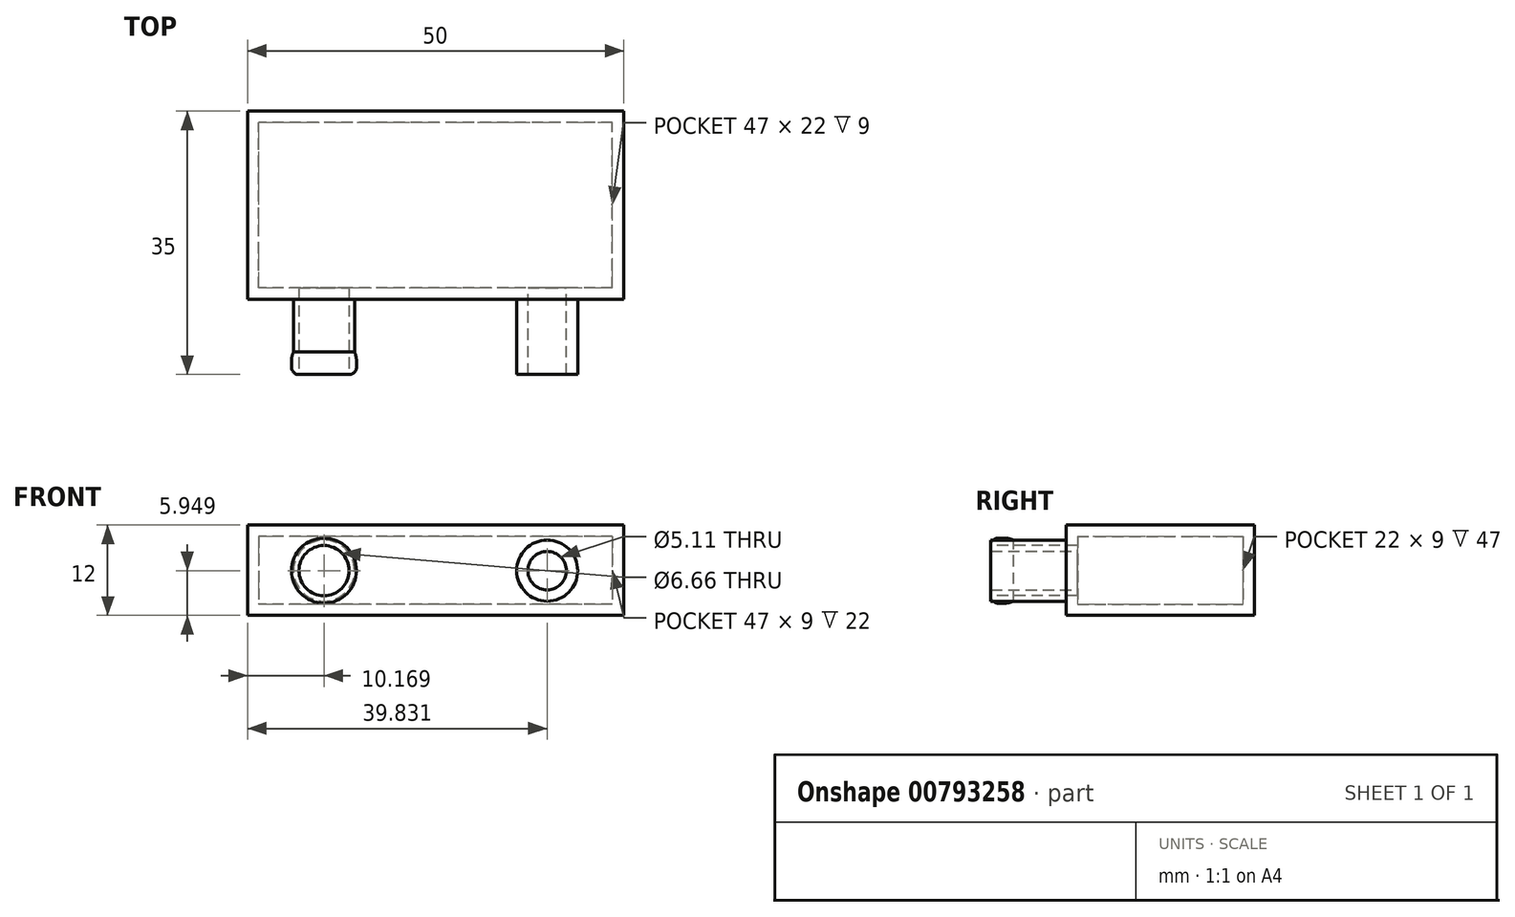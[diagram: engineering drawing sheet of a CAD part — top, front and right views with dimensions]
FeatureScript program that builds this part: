
annotation { "Feature Type Name" : "Feature", "Feature Type Description" : "" }
export const myFeature = defineFeature(function(context is Context, id is Id, definition is map)
    precondition{}
    {
        {
            var Q0;
            Q0=qCreatedBy(makeId("Top.planeOp"),FACE);
            var sketch = newSketch(context, id + "F0", { "sketchPlane" : qUnion([Q0])});
            skLineSegment(sketch, "E0.bottom", {"start": v(25, -12.5) * mm, "end": v(-25, -12.5) * mm});
            skLineSegment(sketch, "E0.top", {"start": v(25, 12.5) * mm, "end": v(-25, 12.5) * mm});
            skLineSegment(sketch, "E0.left", {"start": v(25, -12.5) * mm, "end": v(25, 12.5) * mm});
            skLineSegment(sketch, "E0.right", {"start": v(-25, -12.5) * mm, "end": v(-25, 12.5) * mm});
            skPoint(sketch, "E0.middle", {"position": v(0, 0) * mm});
            skSolve(sketch);
        }
        {
            var Q0;
            Q0 = qSketchRegion(id + "F0", true);
            extrude(context, id + "F1", {"entities" : qUnion([Q0]), "depth" : 12 * mm, "offsetDistance" : 25 * mm});
        }
        {
            var Q0;
            Q0=makeQuery(id+"F1.opExtrude","SWEPT_FACE",FACE,{"disambiguationData":[OSD([sQuery(id+"F0.wireOp",EDGE,"E0.bottom")])]});
            var sketch = newSketch(context, id + "F2", { "sketchPlane" : qUnion([Q0])});
            skCircle(sketch, "E1", {"center": v(-14.83, 5.95) * mm, "radius": 4.05 * mm});
            skLineSegment(sketch, "E2", {"start": v(0, 20.65) * mm, "end": v(0, -15.35) * mm, "construction": true});
            skCircle(sketch, "E3.MirrorC", {"center": v(14.83, 5.95) * mm, "radius": 4.05 * mm});
            skSolve(sketch);
        }
        {
            var Q0;
            Q0 = qSketchRegion(id + "F2", true);
            extrude(context, id + "F3", {"entities" : qUnion([Q0]), "operationType" : NewBodyOperationType.ADD, "depth" : 10 * mm, "offsetDistance" : 25 * mm});
        }
        {
            var Q0;
            Q0=makeQuery(id+"F3.opExtrude","CAP_FACE",FACE,{"disambiguationData":[OSD([sQuery(id+"F2.wireOp",EDGE,"E3.MirrorC")])],"isStart":false});
            var Q1;
            Q1=makeQuery(id+"F3.opExtrude","CAP_FACE",FACE,{"disambiguationData":[OSD([sQuery(id+"F2.wireOp",EDGE,"E1")])],"isStart":false});
            shell(context, id + "F4", {"entities" : qUnion([Q0, Q1]), "thickness" : 1.5 * mm});
        }
        {
            var Q0;
            Q0=makeQuery(id+"F3.opExtrude","CAP_FACE",FACE,{"disambiguationData":[OSD([sQuery(id+"F2.wireOp",EDGE,"E1")])],"isStart":false});
            var sketch = newSketch(context, id + "F5", { "sketchPlane" : qUnion([Q0])});
            skCircle(sketch, "E4", {"center": v(-14.83, 5.95) * mm, "radius": 4.33 * mm});
            skSolve(sketch);
        }
        {
            var Q0;
            Q0 = qSketchRegion(id + "F5", true);
            extrude(context, id + "F6", {"entities" : qUnion([Q0]), "operationType" : NewBodyOperationType.ADD, "oppositeDirection" : true, "depth" : 3 * mm, "offsetDistance" : 25 * mm});
        }
        {
            var Q0;
            Q0=makeQuery(id+"F6.opExtrude","CAP_EDGE",EDGE,{"disambiguationData":[OSD([sQuery(id+"F5.wireOp",EDGE,"E4")])],"isStart":false});
            fillet(context, id + "F7", {"entities" : qUnion([Q0]), "radius" : 3 * mm, "tangentPropagation" : true, "allowEdgeOverflow" : false});
        }
        {
            var Q0;
            Q0=makeQuery(id+"F6.opExtrude","CAP_EDGE",EDGE,{"disambiguationData":[OSD([sQuery(id+"F5.wireOp",EDGE,"E4")])],"isStart":true});
            fillet(context, id + "F8", {"entities" : qUnion([Q0]), "radius" : 1 * mm, "tangentPropagation" : true, "allowEdgeOverflow" : false});
        }
        {
            var Q0;
            Q0=makeQuery(id+"F6.boolean.opBoolean","MERGE",FACE,{"derivedFrom":[makeQuery(id+"F3.opExtrude","CAP_FACE",FACE,{"disambiguationData":[OSD([sQuery(id+"F2.wireOp",EDGE,"E1")])],"isStart":false}),makeQuery(id+"F6.opExtrude","CAP_FACE",FACE,{"disambiguationData":[OSD([sQuery(id+"F5.wireOp",EDGE,"E4")])],"isStart":true})]});
            extrude(context, id + "F9", {"entities" : qUnion([Q0]), "operationType" : NewBodyOperationType.REMOVE, "oppositeDirection" : true, "depth" : 20 * mm, "offsetDistance" : 25 * mm});
        }
    });
